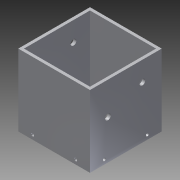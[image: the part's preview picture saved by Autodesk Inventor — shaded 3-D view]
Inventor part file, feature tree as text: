
AUTODESK INVENTOR PART (.ipt)
format: ipt  version: 2013 (Build 170138000, 138)  size: 137,216 bytes
history: native  units: mm
features: sketch x4, hole x3, other x1, extrude x1
ambient origin geometry x1: Origin
feature tree (9):
  other  "ソリッド1"
  extrude  "押し出し1"  Depth=50.0mm
  hole  "穴6"  [1 undecoded]
  hole  "穴16"  [1 undecoded]
  hole  "穴17"  [1 undecoded]
  sketch  "スケッチ1"
  sketch  "スケッチ11"
  sketch  "スケッチ15"
  sketch  "スケッチ16"
note: 3 required parameter values undecoded (feature->parameter linkage not recoverable at this tier; creation-order binding heuristic only, values carry confidence <= 0.55)
